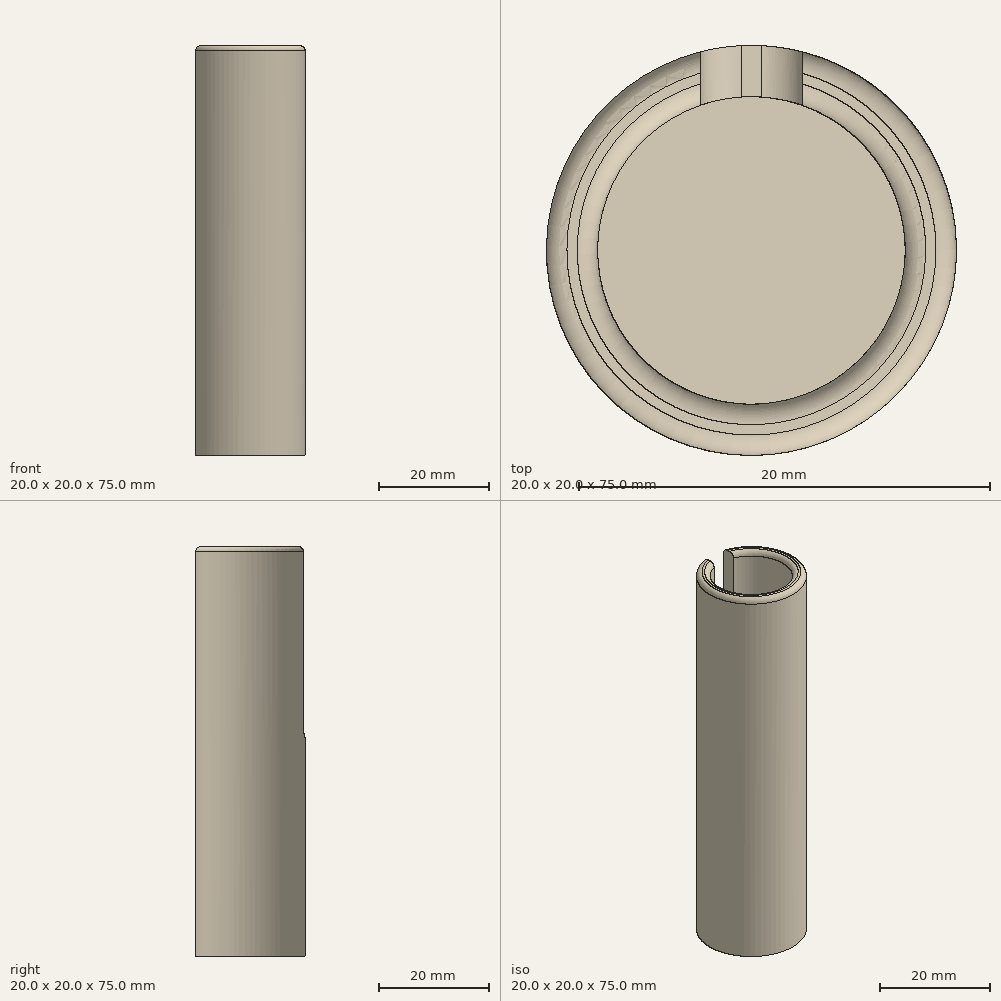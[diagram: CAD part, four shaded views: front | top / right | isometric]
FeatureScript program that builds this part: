
annotation { "Feature Type Name" : "Feature", "Feature Type Description" : "" }
export const myFeature = defineFeature(function(context is Context, id is Id, definition is map)
    precondition{}
    {
        {
            var Q0;
            Q0=qCreatedBy(makeId("Top.planeOp"),FACE);
            var sketch = newSketch(context, id + "F0", { "sketchPlane" : qUnion([Q0])});
            skCircle(sketch, "E0", {"center": v(0, 0) * mm, "radius": 10 * mm});
            skCircle(sketch, "E1", {"center": v(0, 0) * mm, "radius": 7.5 * mm});
            skSolve(sketch);
        }
        {
            var Q0;
            Q0=makeQuery(id+"F0.imprint","IMPRINT",FACE,{"disambiguationData":[TD([[makeQuery(id+"F0.imprint","IMPRINT",EDGE,{"derivedFrom":sQuery(id+"F0.wireOp",EDGE,"E0")}),1.0]])]});
            extrude(context, id + "F1", {"entities" : qUnion([Q0]), "depth" : 45 * mm});
        }
        {
            var Q0;
            Q0 = qSketchRegion(id + "F0", true);
            var Q1;
            Q1=makeQuery(id+"F0.imprint","IMPRINT",FACE,{"disambiguationData":[TD([[makeQuery(id+"F0.imprint","IMPRINT",EDGE,{"derivedFrom":sQuery(id+"F0.wireOp",EDGE,"E1")}),1.0]])]});
            extrude(context, id + "F2", {"entities" : qUnion([Q0, Q1]), "operationType" : NewBodyOperationType.ADD, "depth" : 5 * mm});
        }
        {
            var Q0;
            Q0=qCreatedBy(makeId("Top.planeOp"),FACE);
            var sketch = newSketch(context, id + "F3", { "sketchPlane" : qUnion([Q0])});
            skCircle(sketch, "E2", {"center": v(0, 0) * mm, "radius": 7 * mm});
            skCircle(sketch, "E3", {"center": v(0, 0) * mm, "radius": 10 * mm});
            skCircle(sketch, "E4", {"center": v(0, 0) * mm, "radius": 8.4 * mm});
            skSolve(sketch);
        }
        {
            var Q0;
            Q0 = qSketchRegion(id + "F3", true);
            var Q1;
            Q1=makeQuery(id+"F0.imprint","IMPRINT",FACE,{"disambiguationData":[TD([[makeQuery(id+"F0.imprint","IMPRINT",EDGE,{"derivedFrom":sQuery(id+"F0.wireOp",EDGE,"E1")}),1.0]])]});
            extrude(context, id + "F4", {"entities" : qUnion([Q0, Q1]), "operationType" : NewBodyOperationType.ADD, "oppositeDirection" : true, "depth" : 30 * mm});
        }
        {
            var Q0;
            Q0=makeQuery(id+"F4.opExtrude","CAP_EDGE",EDGE,{"disambiguationData":[OSD([sQuery(id+"F0.wireOp",EDGE,"E1")])],"isStart":false});
            chamfer(context, id + "F5", {"entities" : qUnion([Q0]), "width" : 2 * mm, "tangentPropagation" : true});
        }
        {
            var Q0;
            Q0=makeQuery(id+"F1.opExtrude","CAP_FACE",FACE,{"disambiguationData":[OSD([sQuery(id+"F0.wireOp",EDGE,"E0"),sQuery(id+"F0.wireOp",EDGE,"E1")])],"isStart":false});
            var sketch = newSketch(context, id + "F6", { "sketchPlane" : qUnion([Q0])});
            skLineSegment(sketch, "E5.rect.bottom", {"start": v(-2.5, 16.3) * mm, "end": v(2.5, 16.3) * mm});
            skPoint(sketch, "E5.rect.middle", {"position": v(0, 0) * mm});
            skLineSegment(sketch, "E6.bottom", {"start": v(2.5, 0) * mm, "end": v(-2.5, 0) * mm});
            skLineSegment(sketch, "E6.top", {"start": v(2.5, 16.3) * mm, "end": v(-2.5, 16.3) * mm});
            skLineSegment(sketch, "E6.left", {"start": v(2.5, 0) * mm, "end": v(2.5, 16.3) * mm});
            skLineSegment(sketch, "E6.right", {"start": v(-2.5, 0) * mm, "end": v(-2.5, 16.3) * mm});
            skSolve(sketch);
        }
        {
            var Q0;
            Q0 = qSketchRegion(id + "F6", true);
            extrude(context, id + "F7", {"entities" : qUnion([Q0]), "operationType" : NewBodyOperationType.REMOVE, "oppositeDirection" : true, "depth" : 35 * mm});
        }
        {
            var Q0;
            Q0=makeQuery(id+"F7.boolean.opBoolean","COPY",EDGE,{"derivedFrom":makeQuery(id+"F7.opExtrude","CAP_EDGE",EDGE,{"disambiguationData":[OSD([sQuery(id+"F6.wireOp",EDGE,"E6.left")])],"isStart":false})});
            var Q1;
            Q1=makeQuery(id+"F7.boolean.opBoolean","COPY",EDGE,{"derivedFrom":makeQuery(id+"F7.opExtrude","CAP_EDGE",EDGE,{"disambiguationData":[OSD([sQuery(id+"F6.wireOp",EDGE,"E6.right")])],"isStart":false})});
            fillet(context, id + "F8", {"entities" : qUnion([Q0, Q1]), "radius" : 2 * mm, "tangentPropagation" : true, "allowEdgeOverflow" : false});
        }
        {
            var Q0;
            {var subQ0=sQuery(id+"F0.wireOp",EDGE,"E1");Q0=makeQuery(id+"F7.boolean.opBoolean","SPLIT",EDGE,{"disambiguationData":[TD([makeQuery(id+"F7.opExtrude","SWEPT_FACE",FACE,{"disambiguationData":[OSD([sQuery(id+"F6.wireOp",EDGE,"E5.rect.right")])]})])],"derivedFrom":makeQuery(id+"F1.opExtrude","CAP_EDGE",EDGE,{"disambiguationData":[OSD([subQ0])],"isStart":false})});}
            var Q1;
            {var subQ0=sQuery(id+"F0.wireOp",EDGE,"E1");Q1=makeQuery(id+"F7.boolean.opBoolean","SPLIT",EDGE,{"disambiguationData":[TD([makeQuery(id+"F7.opExtrude","SWEPT_FACE",FACE,{"disambiguationData":[OSD([sQuery(id+"F6.wireOp",EDGE,"E5.rect.left")])]})])],"derivedFrom":makeQuery(id+"F1.opExtrude","CAP_EDGE",EDGE,{"disambiguationData":[OSD([subQ0])],"isStart":false})});}
            var Q2;
            {var subQ0=sQuery(id+"F0.wireOp",EDGE,"E0");Q2=makeQuery(id+"F7.boolean.opBoolean","SPLIT",EDGE,{"disambiguationData":[TD([makeQuery(id+"F7.opExtrude","SWEPT_FACE",FACE,{"disambiguationData":[OSD([sQuery(id+"F6.wireOp",EDGE,"E5.rect.right")])]})])],"derivedFrom":makeQuery(id+"F1.opExtrude","CAP_EDGE",EDGE,{"disambiguationData":[OSD([subQ0])],"isStart":false})});}
            var Q3;
            {var subQ0=sQuery(id+"F0.wireOp",EDGE,"E0");Q3=makeQuery(id+"F7.boolean.opBoolean","SPLIT",EDGE,{"disambiguationData":[TD([makeQuery(id+"F7.opExtrude","SWEPT_FACE",FACE,{"disambiguationData":[OSD([sQuery(id+"F6.wireOp",EDGE,"E5.rect.left")])]})])],"derivedFrom":makeQuery(id+"F1.opExtrude","CAP_EDGE",EDGE,{"disambiguationData":[OSD([subQ0])],"isStart":false})});}
            fillet(context, id + "F9", {"entities" : qUnion([Q0, Q1, Q2, Q3]), "radius" : 1 * mm, "tangentPropagation" : true, "allowEdgeOverflow" : false});
        }
    });
